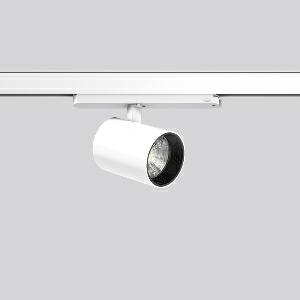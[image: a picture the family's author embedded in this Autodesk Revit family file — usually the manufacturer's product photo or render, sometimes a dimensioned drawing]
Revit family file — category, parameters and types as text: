
# Revit family: deecos_s_mini_track-in_742264_002_3_730_e4b6
name_source: partatom
category: Lighting Fixtures
units: mm (PartAtom-declared; Revit-internal decimal feet)

## family parameters
Cut with Voids When Loaded = No
Host = Face
Light Source = No
Part Type = Normal
Room Calculation Point = No
Round Connector Dimension = Use Diameter
Shared = No

## types (1)
- DEECOS S mini track-in (1 x LED Modul 935, 3300 lm, 3500)
    Apparent Load = 29 VA
    Approval mark = CE
    CIE Flux Codes = 80 99 100 100 100
    Color Rendering = 92
    Color Temperature = 3500
    Default Elevation = 1800 mm
    Description = Series: DEECOS S mini track-in
LED surface-mounted projector in modern design with no visible cooling ribs. Housing: die-cast aluminium, powder-coated. Rotation range: 356°. Swivel range: 90°. Black plastic ring and recessed LED to prevent glare from the side. Optical assembly with lens made of plastic (polycarbonate) for the best homogeneous light distribution - can be changed without tools. Best colour rendering index Ra>90. With multi adaptor for 3-circuit tracks 230 V. Suitable for Track on ceiling, Wall track. Track-in driver integrated into the adapter. High quality converter without flickering and stroboscopic effect. With Casambi smart+free Bluetooth control for wireless network and operation using Android / iOS devices, free app available for download. The following accessories can be mounted without use of tools: interchangeable lenses, decorative glasses, honeycomb louvre, clear and frosted diffusers, white interchangeable plastic ring. 
Colour: traffic white, matt (RAL 9016)
Diameter: 87 mm
Height: 135 mm
Lamp: LED
Socket: without socket
Colour temperature: 3500K
Colour rendering index (CRI): 92
System power: 29 W
Rated luminous flux: 3300 lm
Luminous efficiency: 114 lm/W
Control gear: Dimmable Bluetooth converter
Protection class: II
Type of protection: IP 20
    Height = 135 mm
    Lamp = 1 x LED Modul 935
    Lamp Light Flux = 3300 lm
    Lamp count = 1
    Length = 87 mm
    Lifetime = 50000 h
    Luminous efficacy = 114 lm/W
    Manufacturer = RZB
    ModVariant = No
    Model = 742264.002.3.730
    Mounting Place = Ceiling
    Mounting Type = Rail mounted
    Number of Poles = 1
    OnlyDefault = Yes
    Power Factor = 1
    Product Name = DEECOS S mini track-in
    Product group = Track mounted projectors
    ProductGroupID = 301
    Protection Class = Protection class II
    Protection Degree = IP 20
    RLX_Detail_Level = 1
    RLX_Emergency_Light_Flux = 0 lm
    RLX_Emergency_Type = 0
    RLX_Emergency_Type_DB = No
    RlxData = <blob elided: 35181 chars, md5=84b02668>
    Socket = socket
    Standby Power = 0 W
    System Light Flux = 3300 lm
    System Power = 29 W
    Type Comments = Product without accessories
    Type Image = 742108.002.jpg
    URL = http://relux.com
    VarID = ---
    Voltage = 230 V
    Voltage Range = 220-240 V
    Weight = 0.00 kg
    Width = 0 mm  [stored 0 ft]

note: [stored X ft] marks values corroborated as IEEE doubles in the binary element streams (Revit-internal decimal feet)

## geometry (parser evidence)
native form markers: Blend x4, Sweep x10
no freeform markers — native parametric forms only
